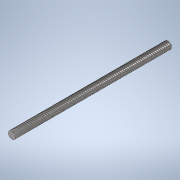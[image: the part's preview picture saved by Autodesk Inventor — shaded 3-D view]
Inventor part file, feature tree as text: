
AUTODESK INVENTOR PART (.ipt)
format: ipt  version: 2020 (Build 240168000, 168)  size: 947,200 bytes
history: native  units: mm
features: sketch x2, extrude x1, helix x1, pattern_circular x1
ambient origin geometry x8: Origin, YZ Plane, XZ Plane, XY Plane, X Axis, Y Axis, Z Axis, Center Point
bodies: Solid1 (feature_tree)
feature tree (5):
  extrude  "Extrusion1"  Depth=8.0mm TaperAngle=0.0deg
  helix  "Coil1"  [1 undecoded]
  pattern_circular  "Circular Pattern1"  Count=4 Angle=360.0deg
  sketch  "Sketch1"  dims[d0=8.0mm d1=170.0mm d2=0.0mm d3=1.0mm]
  sketch  "Sketch2"  dims[d4=3.8mm d5=8.0mm d6=10.0mm d7=212.5mm d8=0.0mm d9=90.0deg d10=90.0deg d11=0.0mm d12=0.0mm d13=40.0mm d14=360.0deg]
note: 1 required parameter value undecoded (feature->parameter linkage not recoverable at this tier; creation-order binding heuristic only, values carry confidence <= 0.55)
